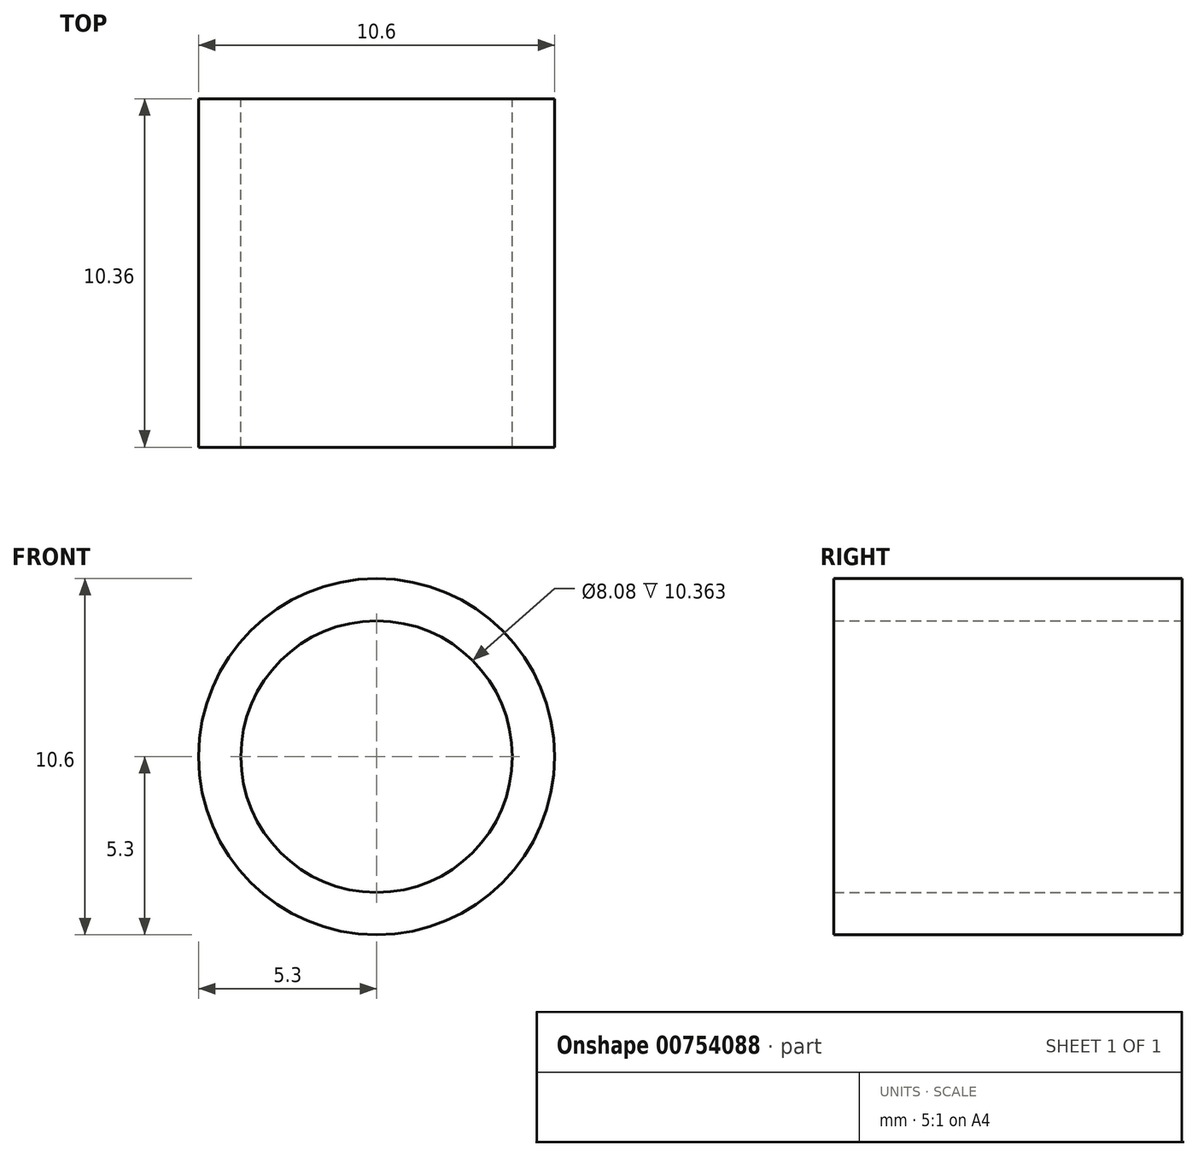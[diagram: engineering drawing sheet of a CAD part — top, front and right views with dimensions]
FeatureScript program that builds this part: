
annotation { "Feature Type Name" : "Feature", "Feature Type Description" : "" }
export const myFeature = defineFeature(function(context is Context, id is Id, definition is map)
    precondition{}
    {
        {
            var Q0;
            Q0=qCreatedBy(makeId("Front.planeOp"),FACE);
            var sketch = newSketch(context, id + "F0", { "sketchPlane" : qUnion([Q0])});
            skCircle(sketch, "E0", {"center": v(0, 0) * mm, "radius": 5.3 * mm});
            skCircle(sketch, "E1", {"center": v(0, 0) * mm, "radius": 4.04 * mm});
            skSolve(sketch);
        }
        {
            var Q0;
            Q0 = qSketchRegion(id + "F0", true);
            extrude(context, id + "F1", {"entities" : qUnion([Q0]), "depth" : 10.36 * mm, "offsetDistance" : 25.4 * mm, "symmetric" : true});
        }
    });
